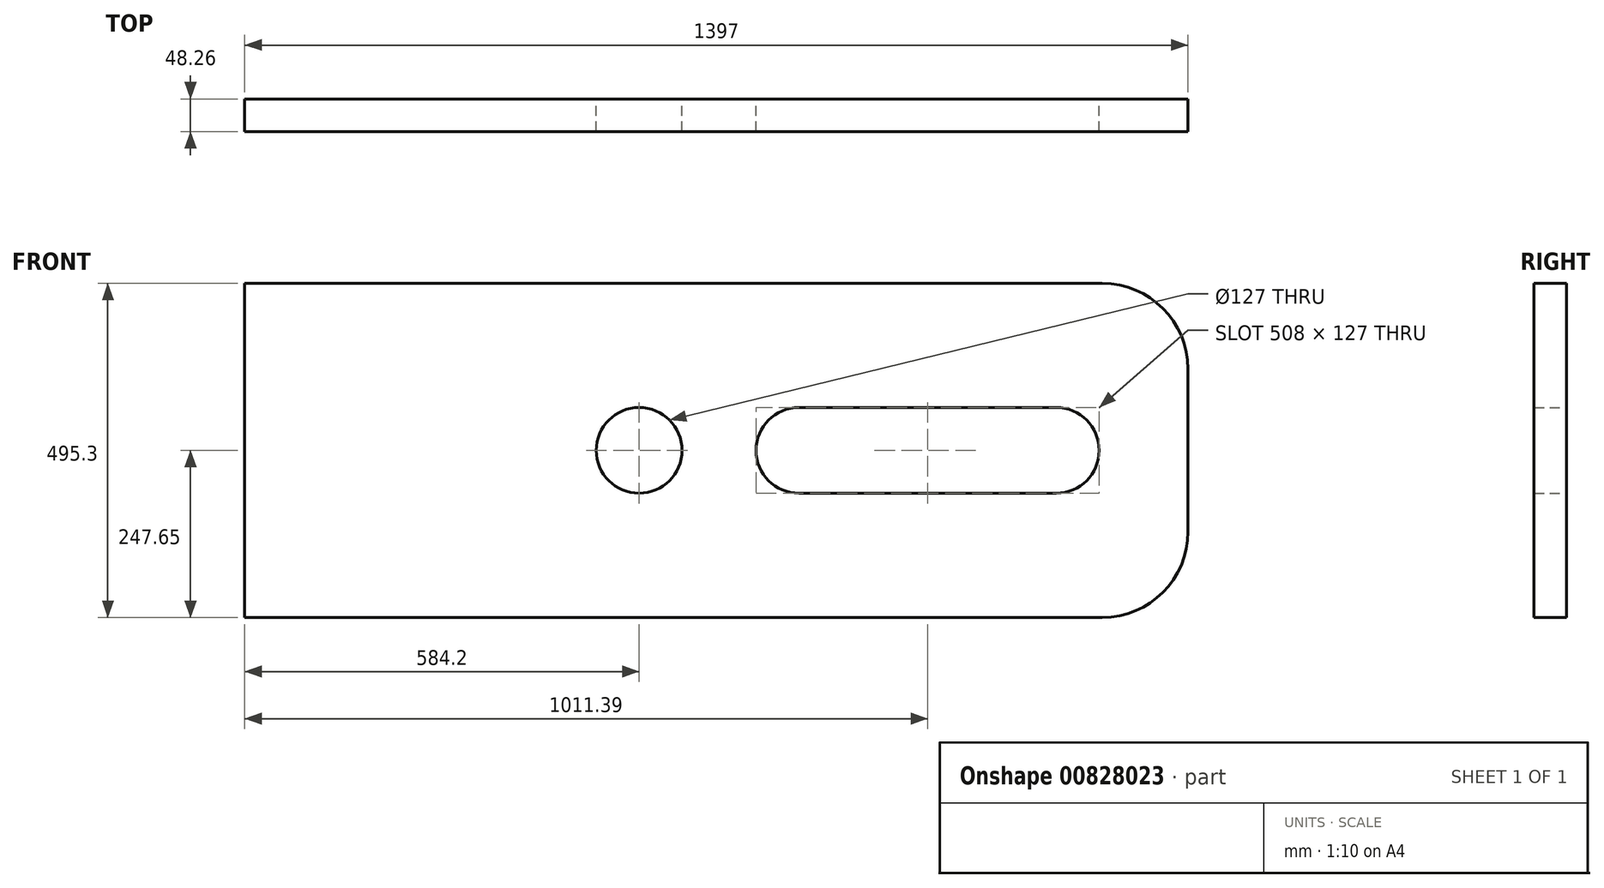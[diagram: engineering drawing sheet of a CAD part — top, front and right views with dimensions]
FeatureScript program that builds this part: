
annotation { "Feature Type Name" : "Feature", "Feature Type Description" : "" }
export const myFeature = defineFeature(function(context is Context, id is Id, definition is map)
    precondition{}
    {
        {
            var Q0;
            Q0=qCreatedBy(makeId("Front.planeOp"),FACE);
            var sketch = newSketch(context, id + "F0", { "sketchPlane" : qUnion([Q0])});
            skLineSegment(sketch, "E0", {"start": v(0, 0) * mm, "end": v(1270, 0) * mm});
            skLineSegment(sketch, "E1", {"start": v(1397, 127) * mm, "end": v(1397, 368.3) * mm});
            skLineSegment(sketch, "E2", {"start": v(1270, 495.3) * mm, "end": v(0, 495.3) * mm});
            skLineSegment(sketch, "E3", {"start": v(0, 495.3) * mm, "end": v(0, 0) * mm});
            skPoint(sketch, "E4.visualSharp", {"position": v(1397, 495.3) * mm});
            skArc(sketch, "E4.filletArc", {"start": v(1397, 368.3) * mm, "mid": v(1359.8, 458.1) * mm, "end": v(1270, 495.3) * mm});
            skPoint(sketch, "E5.visualSharp", {"position": v(1270, 0) * mm});
            skArc(sketch, "E5.filletArc", {"start": v(1270, 0) * mm, "mid": v(1359.8, 37.2) * mm, "end": v(1397, 127) * mm});
            skCircle(sketch, "E6", {"center": v(584.2, 247.65) * mm, "radius": 63.5 * mm});
            skPoint(sketch, "E7.orphan", {"position": v(1168.4, 247.65) * mm});
            skPoint(sketch, "E8.start.orphan", {"position": v(0, 247.65) * mm});
            skLineSegment(sketch, "E9", {"start": v(820.9, 184.15) * mm, "end": v(1201.9, 184.15) * mm});
            skLineSegment(sketch, "E10", {"start": v(820.9, 311.15) * mm, "end": v(1201.9, 311.15) * mm});
            skArc(sketch, "E11", {"start": v(820.9, 311.15) * mm, "mid": v(757.4, 247.65) * mm, "end": v(820.9, 184.15) * mm});
            skArc(sketch, "E12", {"start": v(1201.9, 311.15) * mm, "mid": v(1265.4, 247.65) * mm, "end": v(1201.9, 184.15) * mm});
            skSolve(sketch);
        }
        {
            var Q0;
            Q0 = qSketchRegion(id + "F0", true);
            extrude(context, id + "F1", {"entities" : qUnion([Q0]), "depth" : 48.26 * mm, "offsetDistance" : 25.4 * mm});
        }
    });
